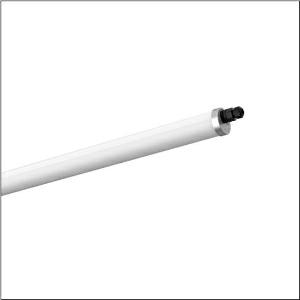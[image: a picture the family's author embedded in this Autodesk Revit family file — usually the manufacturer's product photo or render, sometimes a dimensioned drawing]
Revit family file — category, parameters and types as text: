
# Revit family: monsun_r__31_tube_51ft107n460a_2b58
name_source: partatom
category: Lighting Fixtures
units: mm (PartAtom-declared; Revit-internal decimal feet)

## family parameters
Cut with Voids When Loaded = No
Host = Face
Light Source = No
Part Type = Normal
Room Calculation Point = No
Round Connector Dimension = Use Diameter
Shared = No

## types (1)
- Monsun® 31 Tube (1 x LED, 6500 lm, 40 W, 4000K)
    Apparent Load = 40 VA
    CIE Flux Codes = 42 71 90 91 100
    Color Rendering = 80
    Color Temperature = 4000K
    Default Elevation = 1800 mm
    Description = Monsun® 31 Tube, tubular luminaire, primary optical cover: diffuser, of PMMA, light emission: direct distribution, primary light characteristic: symmetric, installation type: suspended mounting, surface-mounted, LED, rated luminous flux: 6.500lm, luminous efficacy: 160lm/W, light colour: 840, colour temperature: 4000K, with with 1 terminal, 3-pole, max. 2.5mm², through-wiring: 3x 1.5mm², mains connection: 220..240V, AC, 50/60Hz, rated input power: 40W, housing, cylindrical, of PMMA, semi-transparent, matt white, with luminaire and ceiling fastening, V4A, mounting with brackets of stainless steel, length: 1.560mm, diameter: 75mm, end cap, of stainless steel (V4A), protection rating (complete): IP67/IP69K, insulation class (complete): insulation class I (protective earthing), certification: CE, UKCA, impact resistance: IK07, permissible operating ambient temperature: -20..+40°C, corresponds to IFS (International Featured Standards) requirements for safety and quality in the food industry, usage in unprotected outdoor area possible with horizontal mounting, contact your sales advisor before using the luminaires in applications with unclear chemical exposure, large temperature fluctuations or condensation-forming humidity, packaging unit: 1 piece
    Height = 83 mm
    Lamp = 1 x LED
    Lamp Light Flux = 6500 lm
    Lamp Power = 40 W
    Lamp count = 1
    Length = 1560 mm
    Luminous efficacy = 163 lm/W
    Manufacturer = Siteco
    ModVariant = No
    Model = 51FT107N460A
    Mounting Place = Ceiling
    Mounting Type = Pendant
    Number of Poles = 1
    OnlyDefault = Yes
    Power Factor = 1
    Product Name = Monsun® 31 Tube
    Product group = tubular luminaire
    ProductGroupID = 906
    Protection Class = Protection class I
    RLX_Detail_Level = 1
    RLX_Emergency_Light_Flux = 0 lm
    RLX_Emergency_Type = 0
    RLX_Emergency_Type_DB = No
    RlxData = <blob elided: 25321 chars, md5=de4b0cd5>
    Socket = socket
    Standby Power = 0 W
    System Light Flux = 6500 lm
    System Power = 40 W
    Type Comments = Product without accessories
    Type Image = l_1228461.jpg
    URL = http://relux.com
    VarID = ---
    Voltage = 0 V
    Weight = 0.00 kg
    Width = 75 mm

## geometry (parser evidence)
native form markers: Blend x4, Sweep x14
no freeform markers — native parametric forms only
